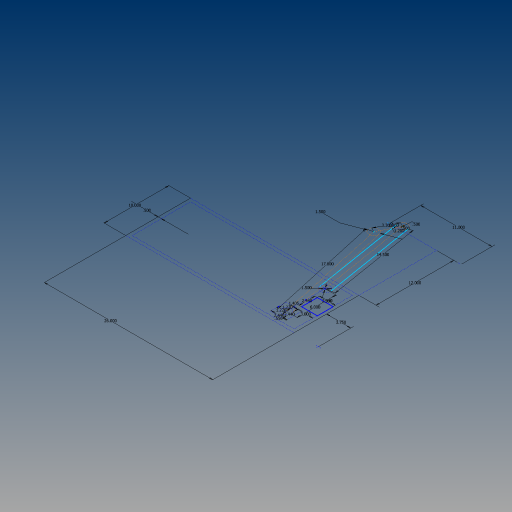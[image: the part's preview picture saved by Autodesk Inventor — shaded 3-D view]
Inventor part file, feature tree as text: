
AUTODESK INVENTOR PART (.ipt)
format: ipt  version: 2024.3 (Build 283343000, 343)  size: 120,832 bytes
history: native  units: in
note: dims shown in document units (in); Inventor stores cm internally (conversion verified against a paired STEP export)
features: sketch x1
ambient origin geometry x8: Origin, YZ Plane, XZ Plane, XY Plane, X Axis, Y Axis, Z Axis, Center Point
feature tree (1):
  sketch  "Sketch1"  dims[d0=26.0in d1=10.0in d2=0.5in d3=3.75in d4=12.0in d5=11.0in d8=1.22in d9=1.22in d10=2.44in d11=2.44in d12=1.2in d15=3.0in d20=3.3in d24=1.0in d30=6.0in d31=0.5563in d34=17.8in d35=14.5in d38=1.405in d39=1.5in d40=0.5in d41=1.5in d42=0.5in d43=0.5in d44=2.44in d45=2.44in]
